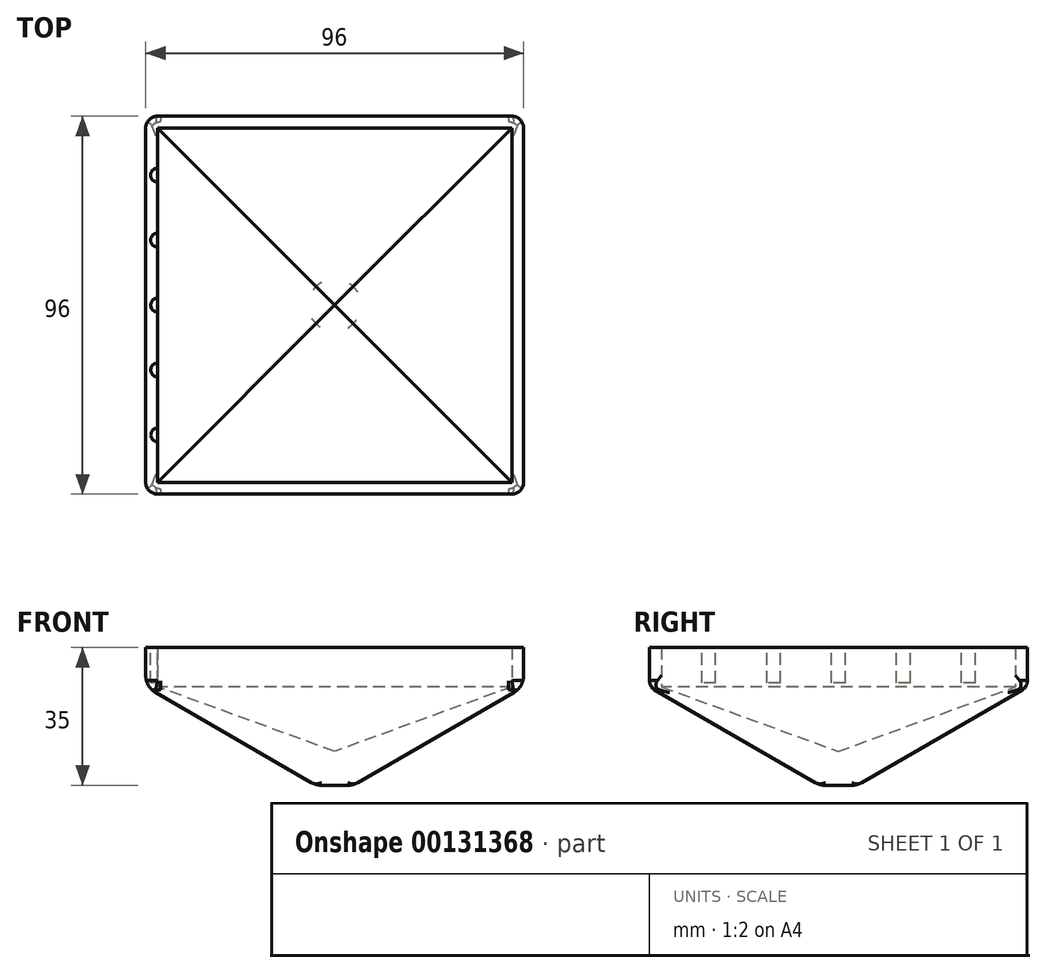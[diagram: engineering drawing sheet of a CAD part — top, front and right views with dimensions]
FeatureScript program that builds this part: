
annotation { "Feature Type Name" : "Feature", "Feature Type Description" : "" }
export const myFeature = defineFeature(function(context is Context, id is Id, definition is map)
    precondition{}
    {
        {
            var Q0;
            Q0=qCreatedBy(makeId("Top.planeOp"),FACE);
            var sketch = newSketch(context, id + "F0", { "sketchPlane" : qUnion([Q0])});
            skLineSegment(sketch, "E0.bottom", {"start": v(-45, 45) * mm, "end": v(45, 45) * mm});
            skLineSegment(sketch, "E0.top", {"start": v(-45, -45) * mm, "end": v(45, -45) * mm});
            skLineSegment(sketch, "E0.left", {"start": v(-45, 45) * mm, "end": v(-45, -45) * mm});
            skLineSegment(sketch, "E0.right", {"start": v(45, 45) * mm, "end": v(45, -45) * mm});
            skLineSegment(sketch, "E1.0", {"start": v(-48, 48) * mm, "end": v(48, 48) * mm});
            skLineSegment(sketch, "E1.1", {"start": v(-48, 48) * mm, "end": v(-48, -48) * mm});
            skLineSegment(sketch, "E1.2", {"start": v(-48, -48) * mm, "end": v(48, -48) * mm});
            skLineSegment(sketch, "E1.3", {"start": v(48, 48) * mm, "end": v(48, -48) * mm});
            skSolve(sketch);
        }
        {
            var Q0;
            Q0=makeQuery(id+"F0.imprint","IMPRINT",FACE,{"disambiguationData":[TD([[makeQuery(id+"F0.imprint","IMPRINT",EDGE,{"derivedFrom":sQuery(id+"F0.wireOp",EDGE,"E0.bottom")}),1.0]])]});
            var Q1;
            Q1=makeQuery(id+"F0.imprint","IMPRINT",FACE,{"disambiguationData":[TD([[makeQuery(id+"F0.imprint","IMPRINT",EDGE,{"derivedFrom":sQuery(id+"F0.wireOp",EDGE,"E0.bottom")}),-1.0]])]});
            extrude(context, id + "F1", {"entities" : qUnion([Q0, Q1]), "oppositeDirection" : true, "depth" : 25 * mm, "hasDraft" : true, "draftAngle" : 60 * degree, "draftPullDirection" : true});
        }
        {
            var Q0;
            Q0=makeQuery(id+"F0.imprint","IMPRINT",FACE,{"disambiguationData":[TD([[makeQuery(id+"F0.imprint","IMPRINT",EDGE,{"derivedFrom":sQuery(id+"F0.wireOp",EDGE,"E0.bottom")}),-1.0]])]});
            extrude(context, id + "F2", {"entities" : qUnion([Q0]), "operationType" : NewBodyOperationType.REMOVE, "oppositeDirection" : true, "depth" : 25 * mm, "hasDraft" : true, "draftAngle" : 70 * degree, "draftPullDirection" : true});
        }
        {
            var Q0;
            Q0=makeQuery(id+"F0.imprint","IMPRINT",FACE,{"disambiguationData":[TD([[makeQuery(id+"F0.imprint","IMPRINT",EDGE,{"derivedFrom":sQuery(id+"F0.wireOp",EDGE,"E0.bottom")}),1.0]])]});
            extrude(context, id + "F3", {"entities" : qUnion([Q0]), "operationType" : NewBodyOperationType.ADD, "depth" : 10 * mm});
        }
        {
            var Q0;
            Q0=makeQuery(id+"F3.opExtrude","CAP_FACE",FACE,{"disambiguationData":[OSD([sQuery(id+"F0.wireOp",EDGE,"E0.bottom"),sQuery(id+"F0.wireOp",EDGE,"E0.top"),sQuery(id+"F0.wireOp",EDGE,"E0.left"),sQuery(id+"F0.wireOp",EDGE,"E0.right"),sQuery(id+"F0.wireOp",EDGE,"E1.0"),sQuery(id+"F0.wireOp",EDGE,"E1.1"),sQuery(id+"F0.wireOp",EDGE,"E1.2"),sQuery(id+"F0.wireOp",EDGE,"E1.3")])],"isStart":false});
            var sketch = newSketch(context, id + "F4", { "sketchPlane" : qUnion([Q0])});
            skCircle(sketch, "E2", {"center": v(-45, 33.02) * mm, "radius": 1.75 * mm});
            skCircle(sketch, "E3.1.0.0", {"center": v(-44.99, 16.52) * mm, "radius": 1.75 * mm});
            skCircle(sketch, "E3.2.0.0", {"center": v(-44.97, 0.02) * mm, "radius": 1.75 * mm});
            skCircle(sketch, "E3.3.0.0", {"center": v(-44.96, -16.48) * mm, "radius": 1.75 * mm});
            skCircle(sketch, "E3.4.0.0", {"center": v(-44.95, -32.98) * mm, "radius": 1.75 * mm});
            skLineSegment(sketch, "E3.direction1", {"start": v(-45, 33.02) * mm, "end": v(-44.99, 16.52) * mm, "construction": true});
            skLineSegment(sketch, "E4.MirrorCS", {"start": v(45, 33.02) * mm, "end": v(44.99, 16.52) * mm, "construction": true});
            skCircle(sketch, "E5.MirrorC", {"center": v(44.95, -32.98) * mm, "radius": 1.75 * mm});
            skCircle(sketch, "E6.MirrorC", {"center": v(44.97, 0.02) * mm, "radius": 1.75 * mm});
            skCircle(sketch, "E7.MirrorC", {"center": v(44.96, -16.48) * mm, "radius": 1.75 * mm});
            skCircle(sketch, "E8.MirrorC", {"center": v(44.99, 16.52) * mm, "radius": 1.75 * mm});
            skCircle(sketch, "E9.MirrorC", {"center": v(45, 33.02) * mm, "radius": 1.75 * mm});
            skSolve(sketch);
        }
        {
            var Q0;
            {var subQ0=sQuery(id+"F4.wireOp",EDGE,"E2");var subQ1=makeQuery(id+"F3.opExtrude","CAP_EDGE",EDGE,{"disambiguationData":[OSD([sQuery(id+"F0.wireOp",EDGE,"E0.left")])],"isStart":false});var subQ2=makeQuery(id+"F4.imprint","INTERSECT",VERTEX,{"disambiguationData":[OD(0.0)],"derivedFrom":[subQ1,subQ0]});Q0=makeQuery(id+"F4.imprint","IMPRINT",FACE,{"disambiguationData":[TD([[makeQuery(id+"F4.imprint","IMPRINT",EDGE,{"disambiguationData":[TD([[subQ2,-1.0]])],"derivedFrom":subQ0}),1.0]])]});}
            var Q1;
            {var subQ0=sQuery(id+"F4.wireOp",EDGE,"E3.1.0.0");var subQ1=makeQuery(id+"F3.opExtrude","CAP_EDGE",EDGE,{"disambiguationData":[OSD([sQuery(id+"F0.wireOp",EDGE,"E0.left")])],"isStart":false});var subQ2=makeQuery(id+"F4.imprint","INTERSECT",VERTEX,{"disambiguationData":[OD(0.0)],"derivedFrom":[subQ1,subQ0]});Q1=makeQuery(id+"F4.imprint","IMPRINT",FACE,{"disambiguationData":[TD([[makeQuery(id+"F4.imprint","IMPRINT",EDGE,{"disambiguationData":[TD([[subQ2,-1.0]])],"derivedFrom":subQ0}),1.0]])]});}
            var Q2;
            {var subQ0=sQuery(id+"F4.wireOp",EDGE,"E3.2.0.0");var subQ1=makeQuery(id+"F3.opExtrude","CAP_EDGE",EDGE,{"disambiguationData":[OSD([sQuery(id+"F0.wireOp",EDGE,"E0.left")])],"isStart":false});var subQ2=makeQuery(id+"F4.imprint","INTERSECT",VERTEX,{"disambiguationData":[OD(0.0)],"derivedFrom":[subQ1,subQ0]});Q2=makeQuery(id+"F4.imprint","IMPRINT",FACE,{"disambiguationData":[TD([[makeQuery(id+"F4.imprint","IMPRINT",EDGE,{"disambiguationData":[TD([[subQ2,-1.0]])],"derivedFrom":subQ0}),1.0]])]});}
            var Q3;
            {var subQ0=sQuery(id+"F4.wireOp",EDGE,"E3.3.0.0");var subQ1=makeQuery(id+"F3.opExtrude","CAP_EDGE",EDGE,{"disambiguationData":[OSD([sQuery(id+"F0.wireOp",EDGE,"E0.left")])],"isStart":false});var subQ2=makeQuery(id+"F4.imprint","INTERSECT",VERTEX,{"disambiguationData":[OD(0.0)],"derivedFrom":[subQ1,subQ0]});Q3=makeQuery(id+"F4.imprint","IMPRINT",FACE,{"disambiguationData":[TD([[makeQuery(id+"F4.imprint","IMPRINT",EDGE,{"disambiguationData":[TD([[subQ2,1.0]])],"derivedFrom":subQ0}),1.0]])]});}
            var Q4;
            {var subQ0=sQuery(id+"F4.wireOp",EDGE,"E3.4.0.0");var subQ1=makeQuery(id+"F3.opExtrude","CAP_EDGE",EDGE,{"disambiguationData":[OSD([sQuery(id+"F0.wireOp",EDGE,"E0.left")])],"isStart":false});var subQ2=makeQuery(id+"F4.imprint","INTERSECT",VERTEX,{"disambiguationData":[OD(0.0)],"derivedFrom":[subQ1,subQ0]});Q4=makeQuery(id+"F4.imprint","IMPRINT",FACE,{"disambiguationData":[TD([[makeQuery(id+"F4.imprint","IMPRINT",EDGE,{"disambiguationData":[TD([[subQ2,1.0]])],"derivedFrom":subQ0}),1.0]])]});}
            var Q5;
            {var subQ0=sQuery(id+"F4.wireOp",EDGE,"E5.MirrorC");var subQ1=makeQuery(id+"F3.opExtrude","CAP_EDGE",EDGE,{"disambiguationData":[OSD([sQuery(id+"F0.wireOp",EDGE,"E0.right")])],"isStart":false});var subQ2=makeQuery(id+"F4.imprint","INTERSECT",VERTEX,{"disambiguationData":[OD(0.0)],"derivedFrom":[subQ1,subQ0]});Q5=makeQuery(id+"F4.imprint","IMPRINT",FACE,{"disambiguationData":[TD([[makeQuery(id+"F4.imprint","IMPRINT",EDGE,{"disambiguationData":[TD([[subQ2,1.0]])],"derivedFrom":subQ0}),-1.0]])]});}
            var Q6;
            {var subQ0=sQuery(id+"F4.wireOp",EDGE,"E7.MirrorC");var subQ1=makeQuery(id+"F3.opExtrude","CAP_EDGE",EDGE,{"disambiguationData":[OSD([sQuery(id+"F0.wireOp",EDGE,"E0.right")])],"isStart":false});var subQ2=makeQuery(id+"F4.imprint","INTERSECT",VERTEX,{"disambiguationData":[OD(0.0)],"derivedFrom":[subQ1,subQ0]});Q6=makeQuery(id+"F4.imprint","IMPRINT",FACE,{"disambiguationData":[TD([[makeQuery(id+"F4.imprint","IMPRINT",EDGE,{"disambiguationData":[TD([[subQ2,1.0]])],"derivedFrom":subQ0}),-1.0]])]});}
            var Q7;
            {var subQ0=sQuery(id+"F4.wireOp",EDGE,"E6.MirrorC");var subQ1=makeQuery(id+"F3.opExtrude","CAP_EDGE",EDGE,{"disambiguationData":[OSD([sQuery(id+"F0.wireOp",EDGE,"E0.right")])],"isStart":false});var subQ2=makeQuery(id+"F4.imprint","INTERSECT",VERTEX,{"disambiguationData":[OD(0.0)],"derivedFrom":[subQ1,subQ0]});Q7=makeQuery(id+"F4.imprint","IMPRINT",FACE,{"disambiguationData":[TD([[makeQuery(id+"F4.imprint","IMPRINT",EDGE,{"disambiguationData":[TD([[subQ2,1.0]])],"derivedFrom":subQ0}),-1.0]])]});}
            var Q8;
            {var subQ0=sQuery(id+"F4.wireOp",EDGE,"E8.MirrorC");var subQ1=makeQuery(id+"F3.opExtrude","CAP_EDGE",EDGE,{"disambiguationData":[OSD([sQuery(id+"F0.wireOp",EDGE,"E0.right")])],"isStart":false});var subQ2=makeQuery(id+"F4.imprint","INTERSECT",VERTEX,{"disambiguationData":[OD(0.0)],"derivedFrom":[subQ1,subQ0]});Q8=makeQuery(id+"F4.imprint","IMPRINT",FACE,{"disambiguationData":[TD([[makeQuery(id+"F4.imprint","IMPRINT",EDGE,{"disambiguationData":[TD([[subQ2,-1.0]])],"derivedFrom":subQ0}),-1.0]])]});}
            var Q9;
            {var subQ0=sQuery(id+"F4.wireOp",EDGE,"E9.MirrorC");var subQ1=makeQuery(id+"F3.opExtrude","CAP_EDGE",EDGE,{"disambiguationData":[OSD([sQuery(id+"F0.wireOp",EDGE,"E0.right")])],"isStart":false});var subQ2=makeQuery(id+"F4.imprint","INTERSECT",VERTEX,{"disambiguationData":[OD(0.0)],"derivedFrom":[subQ1,subQ0]});Q9=makeQuery(id+"F4.imprint","IMPRINT",FACE,{"disambiguationData":[TD([[makeQuery(id+"F4.imprint","IMPRINT",EDGE,{"disambiguationData":[TD([[subQ2,-1.0]])],"derivedFrom":subQ0}),-1.0]])]});}
            extrude(context, id + "F5", {"entities" : qUnion([Q0, Q1, Q2, Q3, Q4, Q5, Q6, Q7, Q8, Q9]), "operationType" : NewBodyOperationType.REMOVE, "oppositeDirection" : true, "depth" : 9 * mm});
        }
        {
            var Q0;
            Q0=makeQuery(id+"F1.opExtrude","SWEPT_FACE",FACE,{"disambiguationData":[OSD([sQuery(id+"F0.wireOp",EDGE,"E1.3")])]});
            var Q1;
            Q1=makeQuery(id+"F1.opExtrude","SWEPT_FACE",FACE,{"disambiguationData":[OSD([sQuery(id+"F0.wireOp",EDGE,"E1.1")])]});
            fillet(context, id + "F6", {"entities" : qUnion([Q0, Q1]), "radius" : 5 * mm, "tangentPropagation" : true, "allowEdgeOverflow" : false});
        }
        {
            var Q0;
            Q0=makeQuery(id+"F3.opExtrude","SWEPT_EDGE",EDGE,{"disambiguationData":[OSD([sQuery(id+"F0.wireOp",EDGE,"E1.1"),sQuery(id+"F0.wireOp",EDGE,"E1.2")])]});
            var Q1;
            Q1=makeQuery(id+"F3.opExtrude","SWEPT_EDGE",EDGE,{"disambiguationData":[OSD([sQuery(id+"F0.wireOp",EDGE,"E1.0"),sQuery(id+"F0.wireOp",EDGE,"E1.1")])]});
            var Q2;
            Q2=makeQuery(id+"F3.opExtrude","SWEPT_EDGE",EDGE,{"disambiguationData":[OSD([sQuery(id+"F0.wireOp",EDGE,"E1.0"),sQuery(id+"F0.wireOp",EDGE,"E1.3")])]});
            var Q3;
            Q3=makeQuery(id+"F3.opExtrude","SWEPT_EDGE",EDGE,{"disambiguationData":[OSD([sQuery(id+"F0.wireOp",EDGE,"E1.2"),sQuery(id+"F0.wireOp",EDGE,"E1.3")])]});
            fillet(context, id + "F7", {"entities" : qUnion([Q0, Q1, Q2, Q3]), "radius" : 3 * mm, "tangentPropagation" : true, "allowEdgeOverflow" : false});
        }
        {
            var Q0;
            Q0=makeQuery(id+"F1.opExtrude","CAP_FACE",FACE,{"disambiguationData":[OSD([sQuery(id+"F0.wireOp",EDGE,"E1.0"),sQuery(id+"F0.wireOp",EDGE,"E1.1"),sQuery(id+"F0.wireOp",EDGE,"E1.2"),sQuery(id+"F0.wireOp",EDGE,"E1.3")])],"isStart":false});
            fillet(context, id + "F8", {"entities" : qUnion([Q0]), "radius" : 5 * mm, "tangentPropagation" : true, "allowEdgeOverflow" : false});
        }
        {
            var Q0;
            {var subQ0=sQuery(id+"F0.wireOp",EDGE,"E1.2");Q0=makeQuery(id+"F3.boolean.opBoolean","MERGE",EDGE,{"derivedFrom":[makeQuery(id+"F1.opExtrude","CAP_EDGE",EDGE,{"disambiguationData":[OSD([subQ0])],"isStart":true}),makeQuery(id+"F3.opExtrude","CAP_EDGE",EDGE,{"disambiguationData":[OSD([subQ0])],"isStart":true})]});}
            var Q1;
            {var subQ0=sQuery(id+"F0.wireOp",EDGE,"E1.0");Q1=makeQuery(id+"F3.boolean.opBoolean","MERGE",EDGE,{"derivedFrom":[makeQuery(id+"F1.opExtrude","CAP_EDGE",EDGE,{"disambiguationData":[OSD([subQ0])],"isStart":true}),makeQuery(id+"F3.opExtrude","CAP_EDGE",EDGE,{"disambiguationData":[OSD([subQ0])],"isStart":true})]});}
            fillet(context, id + "F9", {"entities" : qUnion([Q0, Q1]), "radius" : 2.6 * mm, "tangentPropagation" : true, "allowEdgeOverflow" : false});
        }
    });
